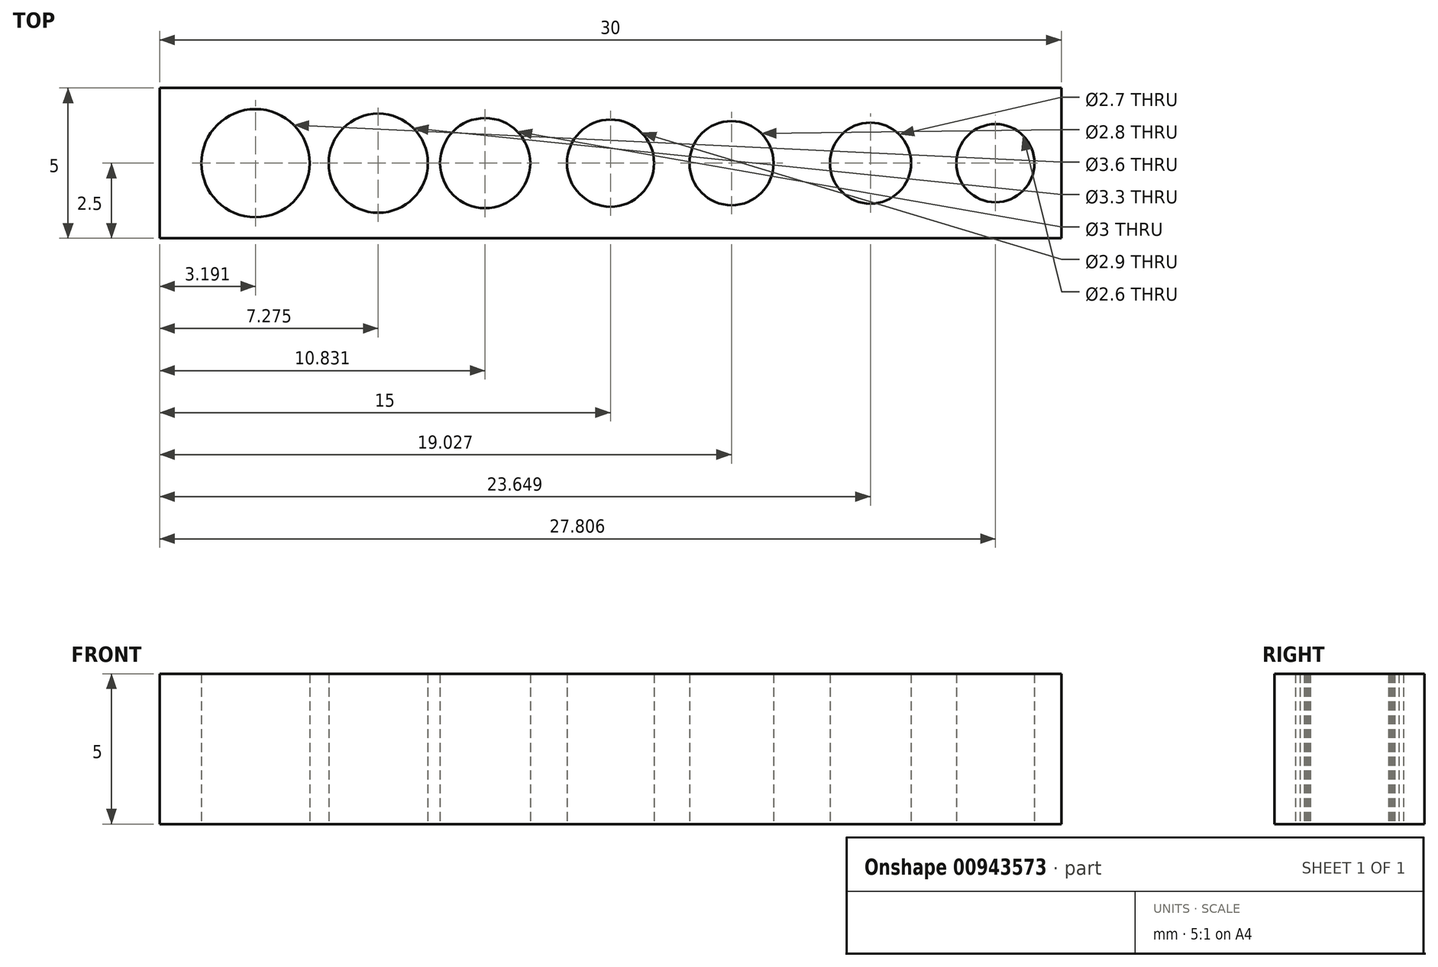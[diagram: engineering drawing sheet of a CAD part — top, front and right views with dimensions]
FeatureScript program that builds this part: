
annotation { "Feature Type Name" : "Feature", "Feature Type Description" : "" }
export const myFeature = defineFeature(function(context is Context, id is Id, definition is map)
    precondition{}
    {
        {
            var Q0;
            Q0=qCreatedBy(makeId("Top.planeOp"),FACE);
            var sketch = newSketch(context, id + "F0", { "sketchPlane" : qUnion([Q0])});
            skLineSegment(sketch, "E0.bottom", {"start": v(15, 2.5) * mm, "end": v(-15, 2.5) * mm});
            skLineSegment(sketch, "E0.top", {"start": v(15, -2.5) * mm, "end": v(-15, -2.5) * mm});
            skLineSegment(sketch, "E0.left", {"start": v(15, 2.5) * mm, "end": v(15, -2.5) * mm});
            skLineSegment(sketch, "E0.right", {"start": v(-15, 2.5) * mm, "end": v(-15, -2.5) * mm});
            skPoint(sketch, "E0.middle", {"position": v(0, 0) * mm});
            skCircle(sketch, "E1", {"center": v(0, 0) * mm, "radius": 1.45 * mm});
            skCircle(sketch, "E2", {"center": v(-4.17, 0) * mm, "radius": 1.5 * mm});
            skCircle(sketch, "E3", {"center": v(-7.72, 0) * mm, "radius": 1.65 * mm});
            skCircle(sketch, "E4", {"center": v(-11.8, 0) * mm, "radius": 1.8 * mm});
            skCircle(sketch, "E5", {"center": v(4.03, 0) * mm, "radius": 1.4 * mm});
            skCircle(sketch, "E6", {"center": v(8.65, 0) * mm, "radius": 1.35 * mm});
            skCircle(sketch, "E7", {"center": v(12.8, 0) * mm, "radius": 1.3 * mm});
            skSolve(sketch);
        }
        {
            var Q0;
            Q0=makeQuery(id+"F0.imprint","IMPRINT",FACE,{"disambiguationData":[TD([[makeQuery(id+"F0.imprint","IMPRINT",EDGE,{"derivedFrom":sQuery(id+"F0.wireOp",EDGE,"E0.bottom")}),1.0]])]});
            extrude(context, id + "F1", {"entities" : qUnion([Q0]), "depth" : 5 * mm, "offsetDistance" : 25 * mm});
        }
    });
